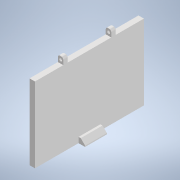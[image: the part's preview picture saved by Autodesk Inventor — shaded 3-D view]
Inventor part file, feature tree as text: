
AUTODESK INVENTOR PART (.ipt)
format: ipt  version: 2020 (Build 240168000, 168)  size: 153,088 bytes
history: native  units: in
note: dims shown in document units (in); Inventor stores cm internally (conversion verified against a paired STEP export)
features: sketch x4, extrude x3, move_body x2, hole x1, chamfer x1, fillet x1
ambient origin geometry x8: Origin, YZ Plane, XZ Plane, XY Plane, X Axis, Y Axis, Z Axis, Center Point
bodies: Solid1 (feature_tree)
feature tree (12):
  extrude  "Extrusion1"  Depth=3.8583in
  move_body  "Move Body1"
  sketch  "Sketch2"  dims[d2=2.6772in d3=0.0in d4=0.625in d5=-0.5625in d6=-15.25in]
  move_body  "Move Body2"
  extrude  "Extrusion2"  Depth=2.6772in
  hole  "Hole1"  [1 undecoded]
  extrude  "Extrusion3"  Depth=0.9843in
  chamfer  "Chamfer1"  Distance=0.5625in
  fillet  "Fillet1"  Radius=0.2362in
  sketch  "Sketch1"  dims[d0=0.1969in d1=3.8583in]
  sketch  "Sketch4"  dims[d7=1.1417in d8=1.1417in]
  sketch  "Sketch5"  dims[d9=0.9843in d10=0.9843in d12=0.0in d13=0.5625in d14=0.0in d15=0.2362in d16=0.0in d17=0.1181in d18=0.0984in d19=0.0984in d20=0.2362in d21=0.1575in d22=0.0787in d23=90.0deg d24=0.315in d25=0.0in d26=0.0394in d27=0.0in d28=0.1969in d29=1.5748in d30=1.5748in d31=0.2362in d32=0.0in d33=0.1575in d34=0.0787in d35=45.0deg d36=0.0984in]
note: 1 required parameter value undecoded (feature->parameter linkage not recoverable at this tier; creation-order binding heuristic only, values carry confidence <= 0.55)
